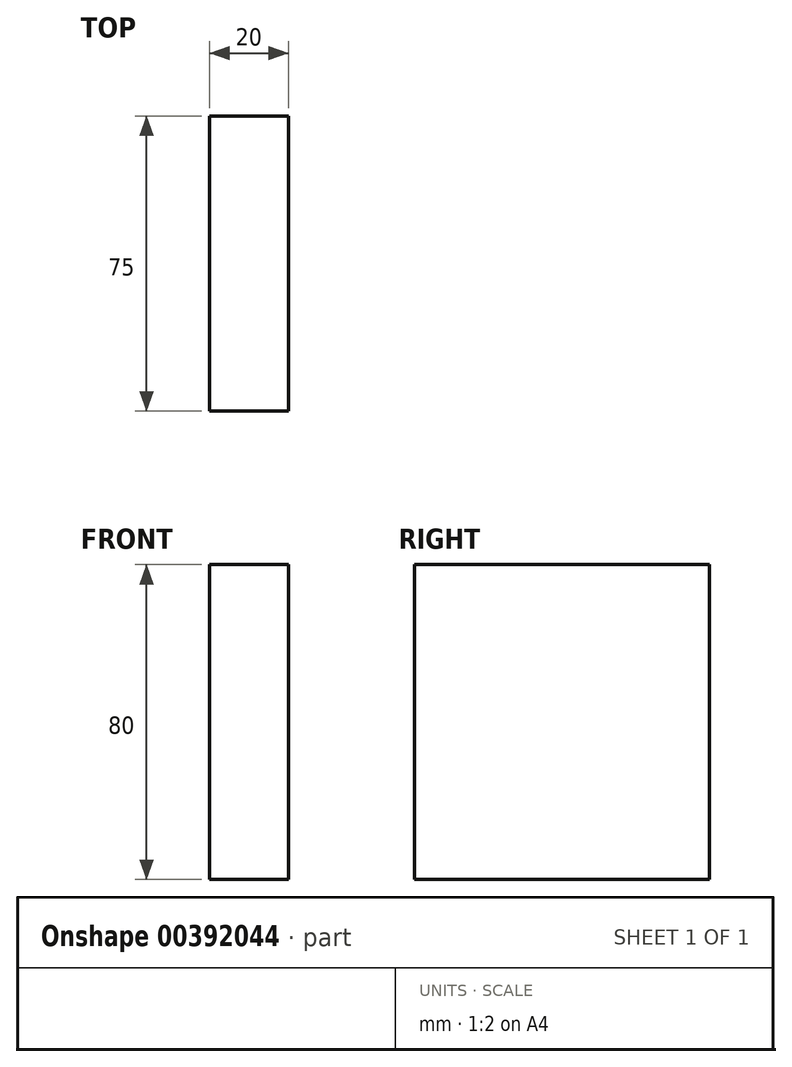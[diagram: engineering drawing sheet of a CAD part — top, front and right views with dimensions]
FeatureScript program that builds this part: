
annotation { "Feature Type Name" : "Feature", "Feature Type Description" : "" }
export const myFeature = defineFeature(function(context is Context, id is Id, definition is map)
    precondition{}
    {
        {
            var Q0;
            Q0=qCreatedBy(makeId("Top.planeOp"),FACE);
            var sketch = newSketch(context, id + "F0", { "sketchPlane" : qUnion([Q0])});
            skLineSegment(sketch, "E0.bottom", {"start": v(-11.83, 57.26) * mm, "end": v(8.17, 57.26) * mm});
            skLineSegment(sketch, "E0.top", {"start": v(-11.83, -17.74) * mm, "end": v(8.17, -17.74) * mm});
            skLineSegment(sketch, "E0.left", {"start": v(-11.83, 57.26) * mm, "end": v(-11.83, -17.74) * mm});
            skLineSegment(sketch, "E0.right", {"start": v(8.17, 57.26) * mm, "end": v(8.17, -17.74) * mm});
            skPoint(sketch, "E0.middle", {"position": v(-1.83, 19.76) * mm});
            skSolve(sketch);
        }
        {
            var Q0;
            Q0 = qSketchRegion(id + "F0", true);
            extrude(context, id + "F1", {"entities" : qUnion([Q0]), "endBound" : BoundingType.SYMMETRIC, "depth" : 80 * mm});
        }
    });
